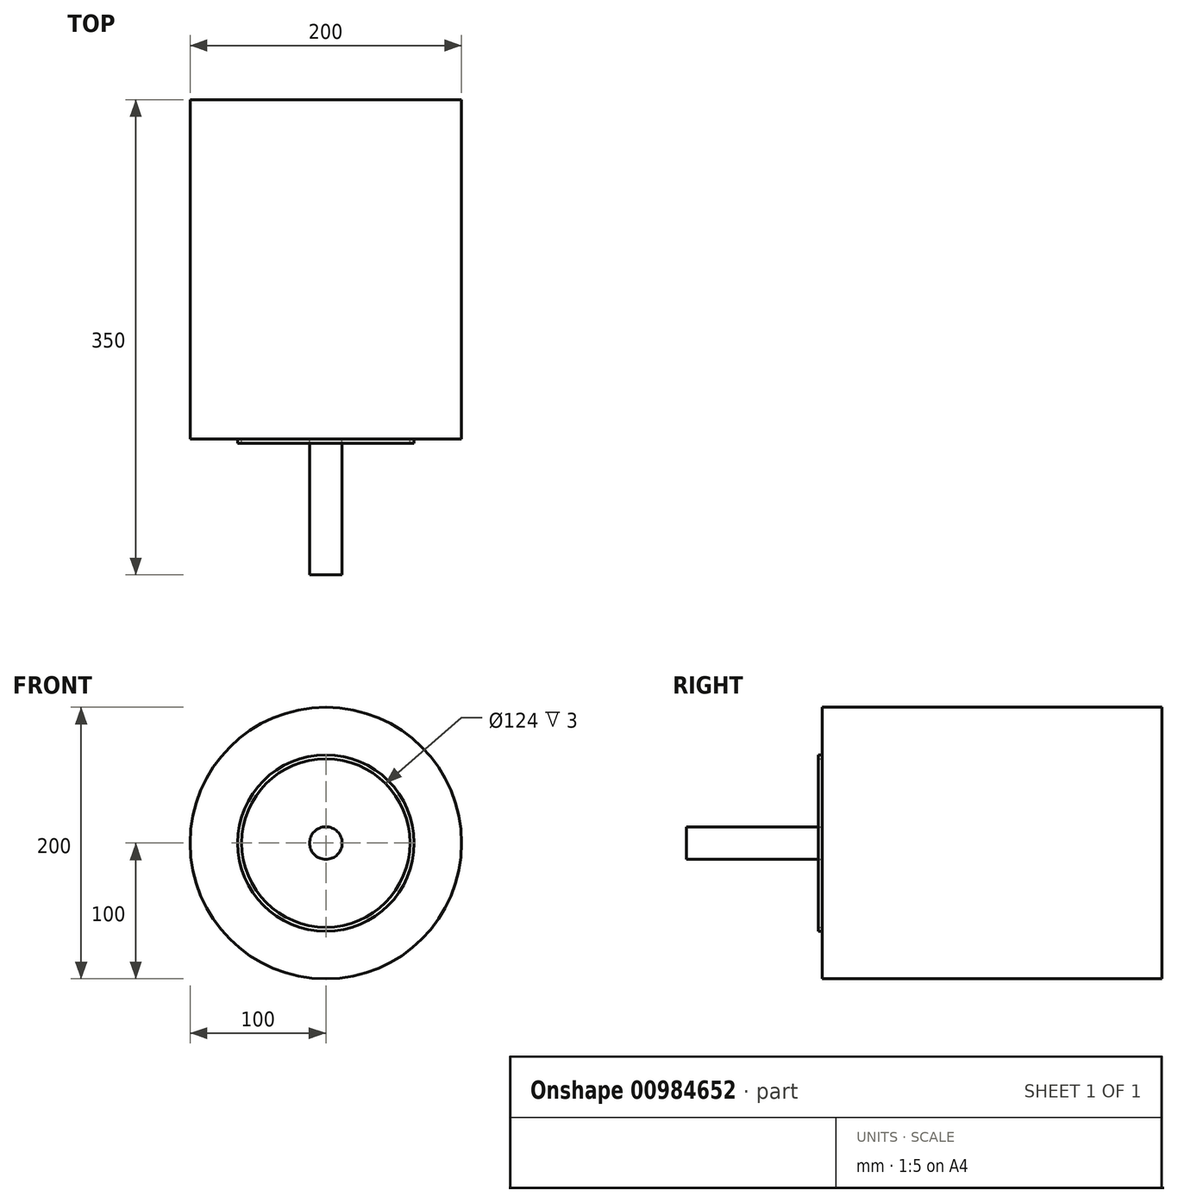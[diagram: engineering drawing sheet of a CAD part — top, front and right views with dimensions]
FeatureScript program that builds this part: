
annotation { "Feature Type Name" : "Feature", "Feature Type Description" : "" }
export const myFeature = defineFeature(function(context is Context, id is Id, definition is map)
    precondition{}
    {
        {
            var Q0;
            Q0=qCreatedBy(makeId("Front.planeOp"),FACE);
            var sketch = newSketch(context, id + "F0", { "sketchPlane" : qUnion([Q0])});
            skCircle(sketch, "E0", {"center": v(0, 0) * mm, "radius": 100 * mm});
            skCircle(sketch, "E1", {"center": v(0, 0) * mm, "radius": 65 * mm});
            skCircle(sketch, "E2", {"center": v(0, 0) * mm, "radius": 62 * mm});
            skCircle(sketch, "E3", {"center": v(0, 0) * mm, "radius": 12 * mm});
            skSolve(sketch);
        }
        {
            var Q0;
            Q0=makeQuery(id+"F0.imprint","IMPRINT",FACE,{"disambiguationData":[TD([[makeQuery(id+"F0.imprint","IMPRINT",EDGE,{"derivedFrom":sQuery(id+"F0.wireOp",EDGE,"E3")}),1.0]])]});
            extrude(context, id + "F1", {"entities" : qUnion([Q0]), "depth" : 100 * mm, "offsetDistance" : 25 * mm});
        }
        {
            var Q0;
            Q0=makeQuery(id+"F0.imprint","IMPRINT",FACE,{"disambiguationData":[TD([[makeQuery(id+"F0.imprint","IMPRINT",EDGE,{"derivedFrom":sQuery(id+"F0.wireOp",EDGE,"E1")}),1.0]])]});
            extrude(context, id + "F2", {"entities" : qUnion([Q0]), "depth" : 3 * mm, "offsetDistance" : 25 * mm});
        }
        {
            var Q0;
            Q0=makeQuery(id+"F0.imprint","IMPRINT",FACE,{"disambiguationData":[TD([[makeQuery(id+"F0.imprint","IMPRINT",EDGE,{"derivedFrom":sQuery(id+"F0.wireOp",EDGE,"E3")}),1.0]])]});
            var Q1;
            Q1=makeQuery(id+"F0.imprint","IMPRINT",FACE,{"disambiguationData":[TD([[makeQuery(id+"F0.imprint","IMPRINT",EDGE,{"derivedFrom":sQuery(id+"F0.wireOp",EDGE,"E2")}),1.0]])]});
            var Q2;
            Q2=makeQuery(id+"F0.imprint","IMPRINT",FACE,{"disambiguationData":[TD([[makeQuery(id+"F0.imprint","IMPRINT",EDGE,{"derivedFrom":sQuery(id+"F0.wireOp",EDGE,"E1")}),1.0]])]});
            var Q3;
            Q3=makeQuery(id+"F0.imprint","IMPRINT",FACE,{"disambiguationData":[TD([[makeQuery(id+"F0.imprint","IMPRINT",EDGE,{"derivedFrom":sQuery(id+"F0.wireOp",EDGE,"E0")}),1.0]])]});
            extrude(context, id + "F3", {"entities" : qUnion([Q0, Q1, Q2, Q3]), "oppositeDirection" : true, "depth" : 250 * mm, "offsetDistance" : 25 * mm});
        }
    });
